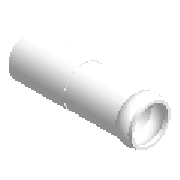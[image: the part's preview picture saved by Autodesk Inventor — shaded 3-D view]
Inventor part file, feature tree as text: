
AUTODESK INVENTOR PART (.ipt)
format: ipt  version: 2023 (Build 270158000, 158)  size: 189,952 bytes
history: native  units: mm (DEFAULTED — no unit token found)
features: other x6, revolve x1, sketch x1
ambient origin geometry x8: Origin, YZ Plane, XZ Plane, XY Plane, X Axis, Y Axis, Z Axis, Center Point
bodies: Solid1 (feature_tree)
feature tree (8):
  revolve  "Revolve1"  [1 undecoded]
  other  "Work Axis1"
  other  "Work Point1"
  other  "Work Point2"
  other  "Work Axis2"
  other  "Work Point3"
  other  "Work Point4"
  sketch  "Sketch1"  dims[d1=160.0mm d2=110.0mm d0=270.5mm d3=160.0mm d4=126.4mm d5=238.0mm d6=21.666667mm d7=30.0deg d8=3.490659mm d9=134.0mm d10=136.2mm d11=110.0mm d12=110.0mm d13=6.5mm d14=238.0mm d15=122.1mm d38=90.0deg d16=6.5mm d17=99.0mm]
note: 1 required parameter value undecoded (feature->parameter linkage not recoverable at this tier; creation-order binding heuristic only, values carry confidence <= 0.55)
